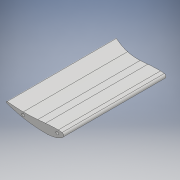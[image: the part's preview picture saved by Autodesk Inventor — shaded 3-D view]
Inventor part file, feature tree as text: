
AUTODESK INVENTOR PART (.ipt)
format: ipt  version: 2018 (Build 220112000, 112)  size: 157,184 bytes
history: native  units: mm
features: other x6, extrude x3, sketch x3, reference x3, projected_geometry x1
ambient origin geometry x8: Origin, YZ Plane, XZ Plane, XY Plane, X Axis, Y Axis, Z Axis, Center Point
bodies: Body1 (feature_tree)
feature tree (16):
  extrude  "押し出し1"  Depth=250.0mm TaperAngle=0.0deg
  extrude  "押し出し2"  Depth=225.0mm TaperAngle=0.0deg
  other  "作業平面2"
  extrude  "押し出し3"  Depth=140.0mm
  other  "ソリッド13"
  sketch  "スケッチ1"
  projected_geometry  "投影ループ1"
  sketch  "スケッチ2"
  other  "作業平面1"
  sketch  "スケッチ3"
  reference  "参照1"
  reference  "参照2"
  reference  "参照3"
  other  "<userpath>\Documents\Inventor\Aero\KS-15\Fr.wing\Fr.wing_assy.iam"
  other  "Fr.wing_assy.iam"
  other  "endplate_ver2:1"
